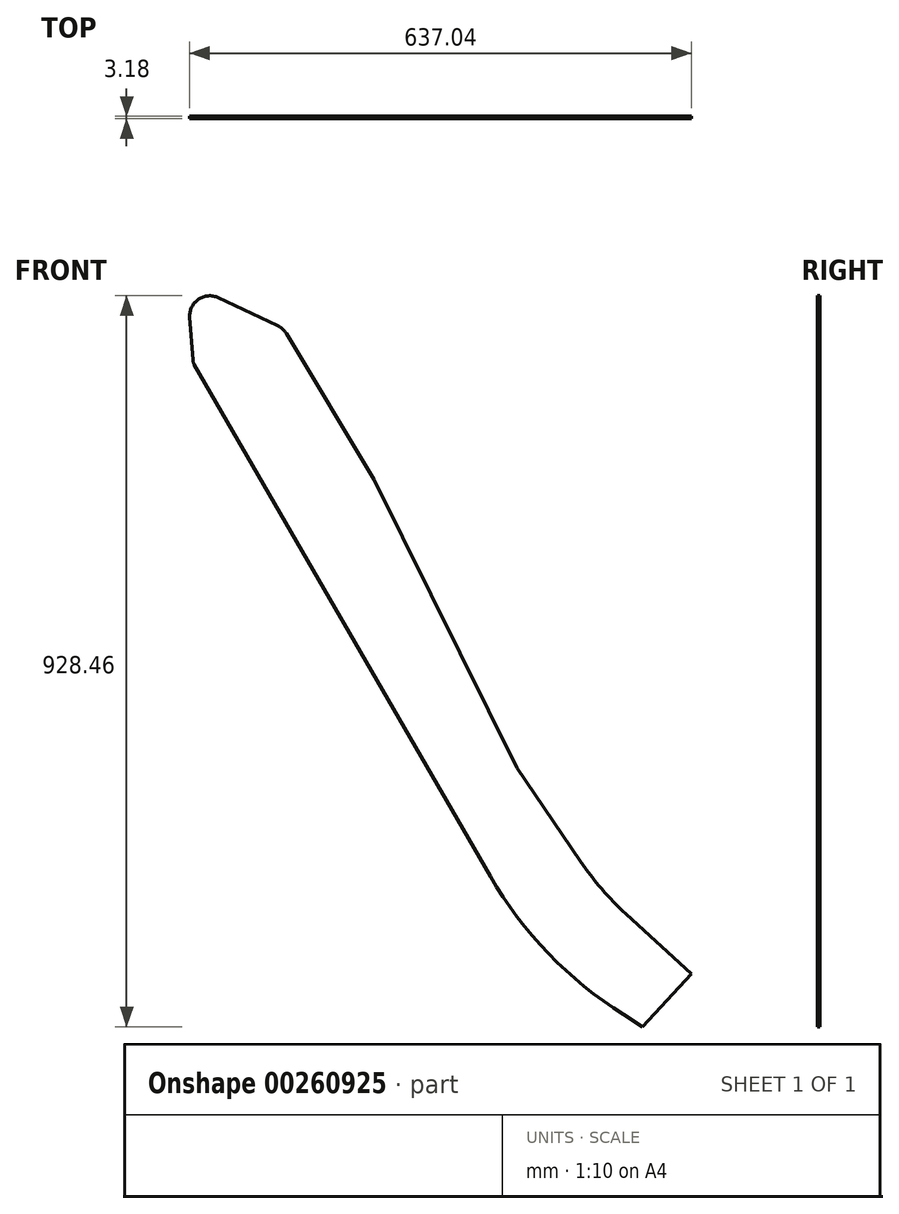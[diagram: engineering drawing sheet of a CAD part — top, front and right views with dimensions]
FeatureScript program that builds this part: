
annotation { "Feature Type Name" : "Feature", "Feature Type Description" : "" }
export const myFeature = defineFeature(function(context is Context, id is Id, definition is map)
    precondition{}
    {
        {
            var Q0;
            Q0=qCreatedBy(makeId("Front.planeOp"),FACE);
            var sketch = newSketch(context, id + "F0", { "sketchPlane" : qUnion([Q0])});
            skLineSegment(sketch, "E0", {"start": v(318.52, -396.97) * mm, "end": v(256.85, -464.23) * mm});
            skLineSegment(sketch, "E1", {"start": v(256.85, -464.23) * mm, "end": v(232.48, -448.89) * mm});
            skArc(sketch, "E2", {"start": v(232.48, -448.89) * mm, "mid": v(137.27, -371.42) * mm, "end": v(63.43, -273.39) * mm});
            skLineSegment(sketch, "E3", {"start": v(63.43, -273.39) * mm, "end": v(-312.78, 376.87) * mm});
            skArc(sketch, "E4", {"start": v(-312.78, 376.87) * mm, "mid": v(-313.93, 379.5) * mm, "end": v(-314.46, 382.3) * mm});
            skLineSegment(sketch, "E5", {"start": v(-314.46, 382.3) * mm, "end": v(-318.45, 436.98) * mm});
            skArc(sketch, "E6", {"start": v(-318.45, 436.98) * mm, "mid": v(-307.5, 459.77) * mm, "end": v(-282.28, 461.8) * mm});
            skLineSegment(sketch, "E7", {"start": v(-282.28, 461.8) * mm, "end": v(-206.74, 426.15) * mm});
            skArc(sketch, "E8", {"start": v(-206.74, 426.15) * mm, "mid": v(-200.54, 422.01) * mm, "end": v(-195.8, 416.26) * mm});
            skLineSegment(sketch, "E9", {"start": v(-195.8, 416.26) * mm, "end": v(-84.33, 230.82) * mm});
            skLineSegment(sketch, "E10", {"start": v(-84.33, 230.82) * mm, "end": v(97.2, -135.72) * mm});
            skLineSegment(sketch, "E11", {"start": v(97.2, -135.72) * mm, "end": v(178.07, -254.48) * mm});
            skArc(sketch, "E12", {"start": v(178.07, -254.48) * mm, "mid": v(204.87, -289.33) * mm, "end": v(235.5, -320.85) * mm});
            skLineSegment(sketch, "E13", {"start": v(235.5, -320.85) * mm, "end": v(318.52, -396.97) * mm});
            skSolve(sketch);
        }
        {
            var Q0;
            Q0 = qSketchRegion(id + "F0", true);
            extrude(context, id + "F1", {"entities" : qUnion([Q0]), "depth" : 3.17 * mm});
        }
    });
